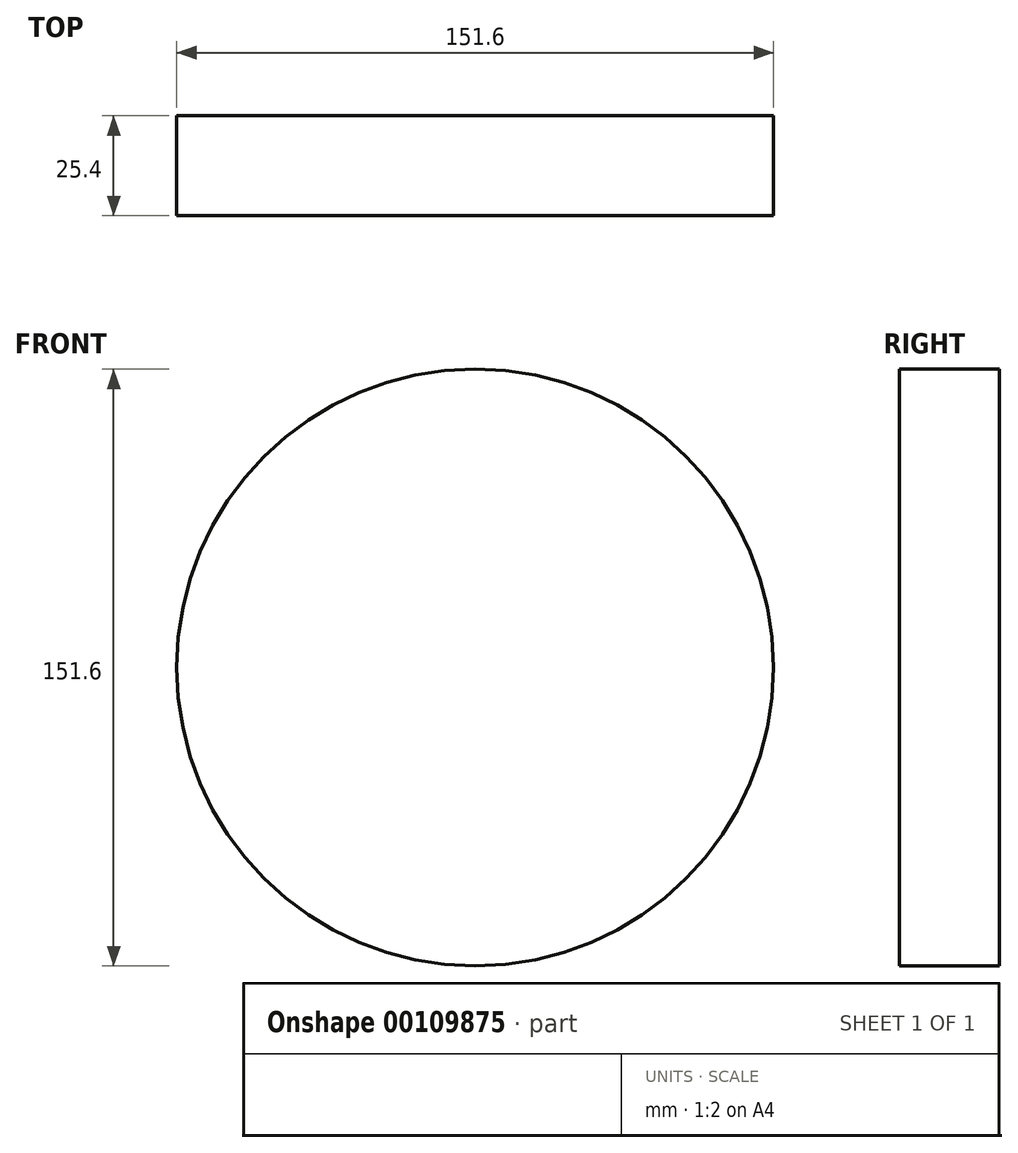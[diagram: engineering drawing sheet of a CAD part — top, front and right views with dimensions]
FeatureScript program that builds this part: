
annotation { "Feature Type Name" : "Feature", "Feature Type Description" : "" }
export const myFeature = defineFeature(function(context is Context, id is Id, definition is map)
    precondition{}
    {
        {
            var Q0;
            Q0=qCreatedBy(makeId("Front.planeOp"),FACE);
            var sketch = newSketch(context, id + "F0", { "sketchPlane" : qUnion([Q0])});
            skCircle(sketch, "E0", {"center": v(0, 0) * mm, "radius": 75.8 * mm});
            skSolve(sketch);
        }
        {
            var Q0;
            Q0 = qSketchRegion(id + "F0", true);
            extrude(context, id + "F1", {"entities" : qUnion([Q0]), "depth" : 25.4 * mm});
        }
    });
